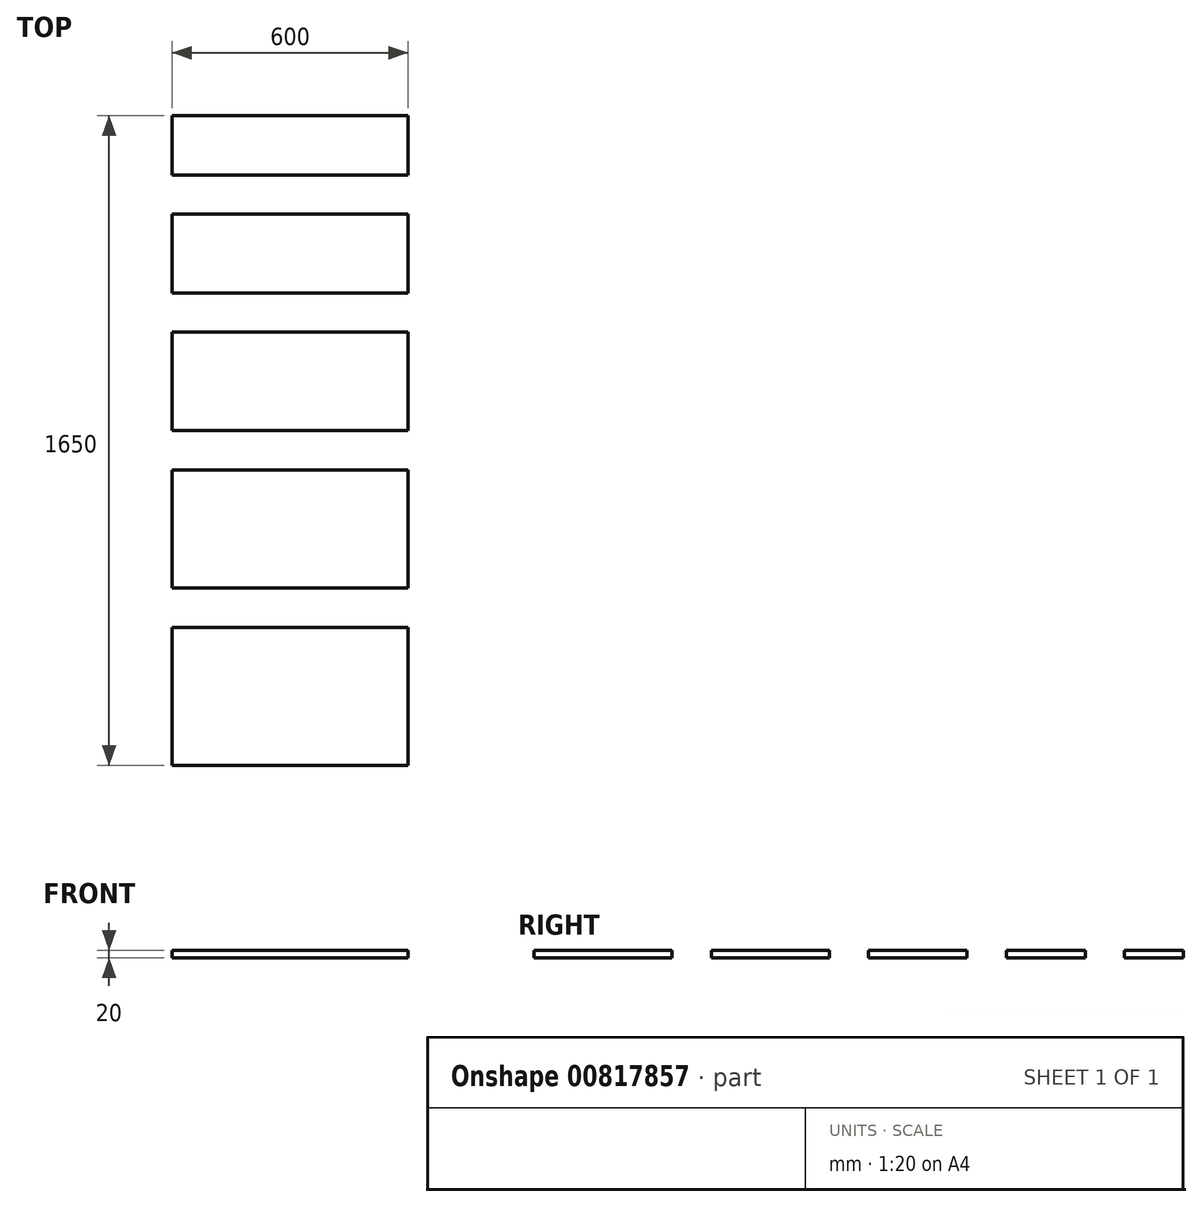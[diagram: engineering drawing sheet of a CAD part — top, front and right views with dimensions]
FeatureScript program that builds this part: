
annotation { "Feature Type Name" : "Feature", "Feature Type Description" : "" }
export const myFeature = defineFeature(function(context is Context, id is Id, definition is map)
    precondition{}
    {
        {
            var Q0;
            Q0=qCreatedBy(makeId("Top.planeOp"),FACE);
            var sketch = newSketch(context, id + "F0", { "sketchPlane" : qUnion([Q0])});
            skLineSegment(sketch, "E0.bottom", {"start": v(0, 0) * mm, "end": v(600, 0) * mm});
            skLineSegment(sketch, "E0.top", {"start": v(0, 350) * mm, "end": v(600, 350) * mm});
            skLineSegment(sketch, "E0.left", {"start": v(0, 0) * mm, "end": v(0, 350) * mm});
            skLineSegment(sketch, "E0.right", {"start": v(600, 0) * mm, "end": v(600, 350) * mm});
            skLineSegment(sketch, "E1.bottom", {"start": v(0, 450) * mm, "end": v(600, 450) * mm});
            skLineSegment(sketch, "E1.top", {"start": v(0, 750) * mm, "end": v(600, 750) * mm});
            skLineSegment(sketch, "E1.left", {"start": v(0, 450) * mm, "end": v(0, 750) * mm});
            skLineSegment(sketch, "E1.right", {"start": v(600, 450) * mm, "end": v(600, 750) * mm});
            skLineSegment(sketch, "E2.bottom", {"start": v(0, 850) * mm, "end": v(600, 850) * mm});
            skLineSegment(sketch, "E2.top", {"start": v(0, 1100) * mm, "end": v(600, 1100) * mm});
            skLineSegment(sketch, "E2.left", {"start": v(0, 850) * mm, "end": v(0, 1100) * mm});
            skLineSegment(sketch, "E2.right", {"start": v(600, 850) * mm, "end": v(600, 1100) * mm});
            skLineSegment(sketch, "E3.bottom", {"start": v(0, 1200) * mm, "end": v(600, 1200) * mm});
            skLineSegment(sketch, "E3.top", {"start": v(0, 1400) * mm, "end": v(600, 1400) * mm});
            skLineSegment(sketch, "E3.left", {"start": v(0, 1200) * mm, "end": v(0, 1400) * mm});
            skLineSegment(sketch, "E3.right", {"start": v(600, 1200) * mm, "end": v(600, 1400) * mm});
            skLineSegment(sketch, "E4.bottom", {"start": v(0, 1500) * mm, "end": v(600, 1500) * mm});
            skLineSegment(sketch, "E4.top", {"start": v(0, 1650) * mm, "end": v(600, 1650) * mm});
            skLineSegment(sketch, "E4.left", {"start": v(0, 1500) * mm, "end": v(0, 1650) * mm});
            skLineSegment(sketch, "E4.right", {"start": v(600, 1500) * mm, "end": v(600, 1650) * mm});
            skSolve(sketch);
        }
        {
            var Q0;
            Q0=makeQuery(id+"F0.imprint","IMPRINT",FACE,{"disambiguationData":[TD([[makeQuery(id+"F0.imprint","IMPRINT",EDGE,{"derivedFrom":sQuery(id+"F0.wireOp",EDGE,"E0.bottom")}),1.0]])]});
            extrude(context, id + "F1", {"entities" : qUnion([Q0]), "depth" : 20 * mm, "offsetDistance" : 25 * mm});
        }
        {
            var Q0;
            Q0=makeQuery(id+"F0.imprint","IMPRINT",FACE,{"disambiguationData":[TD([[makeQuery(id+"F0.imprint","IMPRINT",EDGE,{"derivedFrom":sQuery(id+"F0.wireOp",EDGE,"E1.bottom")}),1.0]])]});
            extrude(context, id + "F2", {"entities" : qUnion([Q0]), "depth" : 20 * mm, "offsetDistance" : 25 * mm});
        }
        {
            var Q0;
            Q0=makeQuery(id+"F0.imprint","IMPRINT",FACE,{"disambiguationData":[TD([[makeQuery(id+"F0.imprint","IMPRINT",EDGE,{"derivedFrom":sQuery(id+"F0.wireOp",EDGE,"E2.bottom")}),1.0]])]});
            extrude(context, id + "F3", {"entities" : qUnion([Q0]), "depth" : 20 * mm, "offsetDistance" : 25 * mm});
        }
        {
            var Q0;
            Q0=makeQuery(id+"F0.imprint","IMPRINT",FACE,{"disambiguationData":[TD([[makeQuery(id+"F0.imprint","IMPRINT",EDGE,{"derivedFrom":sQuery(id+"F0.wireOp",EDGE,"E3.bottom")}),1.0]])]});
            extrude(context, id + "F4", {"entities" : qUnion([Q0]), "depth" : 20 * mm, "offsetDistance" : 25 * mm});
        }
        {
            var Q0;
            Q0=makeQuery(id+"F0.imprint","IMPRINT",FACE,{"disambiguationData":[TD([[makeQuery(id+"F0.imprint","IMPRINT",EDGE,{"derivedFrom":sQuery(id+"F0.wireOp",EDGE,"E4.bottom")}),1.0]])]});
            extrude(context, id + "F5", {"entities" : qUnion([Q0]), "depth" : 20 * mm, "offsetDistance" : 25 * mm});
        }
    });
